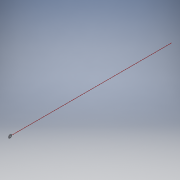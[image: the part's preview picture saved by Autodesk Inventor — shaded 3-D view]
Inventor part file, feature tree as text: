
AUTODESK INVENTOR PART (.ipt)
format: ipt  version: 2016 (Build 200138000, 138)  size: 122,368 bytes
history: native  units: mm
features: sketch x4, reference x4, extrude x2, hole x2, fillet x1
ambient origin geometry x8: Origin, YZ Plane, XZ Plane, XY Plane, X Axis, Y Axis, Z Axis, Center Point
bodies: Solid1 (feature_tree)
feature tree (13):
  extrude  "Extrusion1"  Depth=1200.0mm TaperAngle=0.0deg
  extrude  "Extrusion2"  Depth=25.0mm
  fillet  "Fillet1"  Radius=25.0mm
  hole  "Hole1"  [1 undecoded]
  hole  "Hole2"  [1 undecoded]
  sketch  "Sketch1"  dims[d0=2.0mm d1=1200.0mm d2=0.0mm]
  sketch  "Sketch2"  dims[d3=2.0mm d4=25.0mm d5=25.0mm d6=0.0mm]
  sketch  "Sketch3"  dims[d7=10.0mm d8=6.0mm]
  sketch  "Sketch4"  dims[d9=6.0mm d10=6.0mm d11=4.0mm d12=2.0mm d13=90.0deg d14=8.0mm d15=20.594885mm d16=4.0mm d17=6.0mm d18=4.0mm d19=2.0mm d20=90.0deg d21=8.0mm d22=20.594885mm]
  reference  "Reference1"
  reference  "Reference2"
  reference  "Reference3"
  reference  "Reference4"
note: 2 required parameter values undecoded (feature->parameter linkage not recoverable at this tier; creation-order binding heuristic only, values carry confidence <= 0.55)
